# Revit family: C651Q
name_source: partatom
category: Generic Models
revit_build: Autodesk Revit Architecture 2014 (Build: 20130308_1515(x64)
units: mm (PartAtom-declared; Revit-internal decimal feet)

## types (1)
- C651Q
    CONNECTIVITY- Input Terminals- Analog = None
    CONNECTIVITY- Input Terminals- Audio = 3.5mm Mini Jack , HDMI Audio x3, DisplayPort Audio x2
    CONNECTIVITY- Input Terminals- Data = microSD (Media Player), USB 2.0 (Media Player), USB 2.0 (Service), USB Type-B (Upstream), USB 2.0 x2 (Compute Module, USB CM1 is Powered 5V/2A)
    CONNECTIVITY- Input Terminals- Digital = HDMI 2.0 x3 (with HDCP), DisplayPort 1.2 x2 (with HDCP)
    CONNECTIVITY- Input Terminals- External Control = LAN (100Mbit), 3.5 Mini Jack IR Remote, RS232C
    CONNECTIVITY- Output Terminals- Audio = 3.5mm Audio Mini Jack, External Speaker x2
    CONNECTIVITY- Output Terminals- Digital = DisplayPort (Outputs DisplayPort1 and OPS (1CH DisplayPort Only))
    CONNECTIVITY- Output Terminals- External Control = LAN (100Mb)
    Description = NEC Ultra High Definition Large Format Display
    ENVIRONMENTAL CONDITIONS- Operating Altitude = 3000m (9843ft)
    ENVIRONMENTAL CONDITIONS- Operating Humidity = 20-80%
    ENVIRONMENTAL CONDITIONS- Operating Temperature = 0 to 40C
    LCD MODULE- Aspect Ratio = 16:9
    LCD MODULE- Brightness (Typical/Maximum) = 320/400 cd/m2
    LCD MODULE- Contrast Ratio (Typical) = 4000:1
    LCD MODULE- Displayable Colors = Over 1.07 Billion
    LCD MODULE- Native Resolution = 3840 x 2160
    LCD MODULE- Orientation = Landscape and Portrait
    LCD MODULE- Panel Haze (%) = 44
    LCD MODULE- Panel Technology = D-LED, VA
    LCD MODULE- Viewable Image Size = 65"
    LCD MODULE- Viewing Angle = 178° Vert., 178° Hor. (89U/89D/89L/89R) @ CR>10
    Manufacturer = NEC Display Solutions
    Model = C651Q
    PHYSICAL SPECS- Bezel Width (L/R, T/B) = 12.9mm/12.9mm, 13.1mm/13.1mm
    PHYSICAL SPECS- Net Dimensions (w/o Stand, WxHxD) = 57.34 x 32.7 x 3.1in. 1457.0 x 831.6 x 79.4mm
    PHYSICAL SPECS- Net Weight (w/o Stand) = 89.9lbs / 40.8kg
    PHYSICAL SPECS- Vesa Hole Configuration = 8x M8 x 16mm (600 x 400, 400 x 400)
    POWER CONSUMPTION- Current Rating = 4.3A @ 100V, 1.8A @ 240W
    POWER CONSUMPTION- Network Standby = 2W
    POWER CONSUMPTION- Normal Standby = 0.5W
    POWER CONSUMPTION- On (Typ/Max Bightness/Overall Max) = 200W/255W/365W
    POWER CONSUMPTION- Speaker Rating = Integrated 10W x 2, Optional 15W x 2
    SENSORS- Ambient Light Sensor = Integrated and programmable
    SENSORS- Human Sensor = Optional through KT-RC2 Accessory
    SENSORS- NFC Sensor = Integrated; works in conjunction with free NEC Intelligent Wireless Data Application
    SENSORS- Temperature Sensor = Integrated and programmable; linked to cooling fans
    URL = www.necdisplay.com

## geometry (parser evidence)
native form markers: Blend x1, Sweep x1
no freeform markers — native parametric forms only
